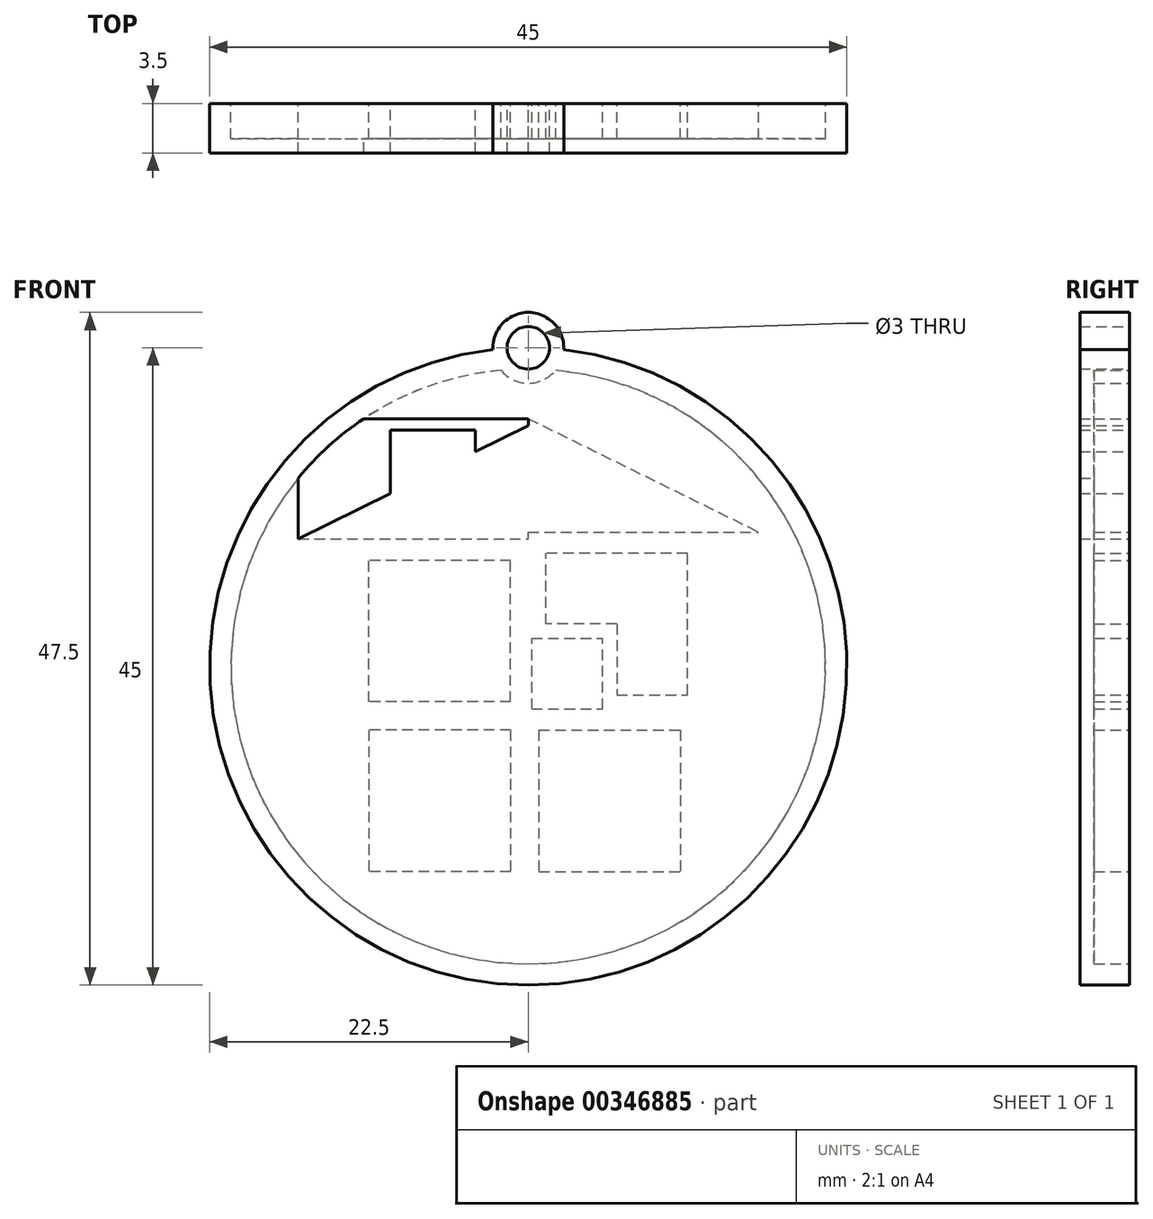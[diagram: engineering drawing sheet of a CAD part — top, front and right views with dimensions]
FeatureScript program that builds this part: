
annotation { "Feature Type Name" : "Feature", "Feature Type Description" : "" }
export const myFeature = defineFeature(function(context is Context, id is Id, definition is map)
    precondition{}
    {
        {
            var Q0;
            Q0=qCreatedBy(makeId("Front.planeOp"),FACE);
            var sketch = newSketch(context, id + "F0", { "sketchPlane" : qUnion([Q0])});
            skLineSegment(sketch, "E0.bottom", {"start": v(0, 0) * mm, "end": v(-10, 0) * mm});
            skLineSegment(sketch, "E0.top", {"start": v(0, 10) * mm, "end": v(-10, 10) * mm});
            skLineSegment(sketch, "E0.left", {"start": v(0, 0) * mm, "end": v(0, 10) * mm});
            skLineSegment(sketch, "E0.right", {"start": v(-10, 0) * mm, "end": v(-10, 10) * mm});
            skLineSegment(sketch, "E1", {"start": v(0, 0) * mm, "end": v(0, -2) * mm});
            skLineSegment(sketch, "E2.bottom", {"start": v(0, -2) * mm, "end": v(-10, -2) * mm});
            skLineSegment(sketch, "E2.top", {"start": v(0, -12) * mm, "end": v(-10, -12) * mm});
            skLineSegment(sketch, "E2.left", {"start": v(0, -2) * mm, "end": v(0, -12) * mm});
            skLineSegment(sketch, "E2.right", {"start": v(-10, -2) * mm, "end": v(-10, -12) * mm});
            skLineSegment(sketch, "E3", {"start": v(0, -2) * mm, "end": v(2, -2) * mm});
            skLineSegment(sketch, "E4.bottom", {"start": v(2, -2) * mm, "end": v(12, -2) * mm});
            skLineSegment(sketch, "E4.top", {"start": v(2, -12) * mm, "end": v(12, -12) * mm});
            skLineSegment(sketch, "E4.left", {"start": v(2, -2) * mm, "end": v(2, -12) * mm});
            skLineSegment(sketch, "E4.right", {"start": v(12, -2) * mm, "end": v(12, -12) * mm});
            skLineSegment(sketch, "E5", {"start": v(2, -2) * mm, "end": v(2, -0.5) * mm});
            skLineSegment(sketch, "E6", {"start": v(0, 0) * mm, "end": v(1.5, 0) * mm});
            skLineSegment(sketch, "E7", {"start": v(1.5, 0) * mm, "end": v(1.5, -0.5) * mm});
            skLineSegment(sketch, "E8", {"start": v(1.5, -0.5) * mm, "end": v(2, -0.5) * mm});
            skLineSegment(sketch, "E9.bottom", {"start": v(1.5, -0.5) * mm, "end": v(6.5, -0.5) * mm});
            skLineSegment(sketch, "E9.top", {"start": v(1.5, 4.5) * mm, "end": v(6.5, 4.5) * mm});
            skLineSegment(sketch, "E9.left", {"start": v(1.5, -0.5) * mm, "end": v(1.5, 4.5) * mm});
            skLineSegment(sketch, "E9.right", {"start": v(6.5, -0.5) * mm, "end": v(6.5, 4.5) * mm});
            skLineSegment(sketch, "E10", {"start": v(6.5, 4.5) * mm, "end": v(7.5, 4.5) * mm});
            skLineSegment(sketch, "E11", {"start": v(7.5, 4.5) * mm, "end": v(7.5, 5.5) * mm});
            skLineSegment(sketch, "E12.bottom", {"start": v(7.5, 5.5) * mm, "end": v(12.5, 5.5) * mm});
            skLineSegment(sketch, "E12.top", {"start": v(7.5, 10.5) * mm, "end": v(12.5, 10.5) * mm});
            skLineSegment(sketch, "E12.left", {"start": v(7.5, 5.5) * mm, "end": v(7.5, 10.5) * mm});
            skLineSegment(sketch, "E12.right", {"start": v(12.5, 5.5) * mm, "end": v(12.5, 10.5) * mm});
            skLineSegment(sketch, "E13.top", {"start": v(7.5, 0.5) * mm, "end": v(12.5, 0.5) * mm});
            skLineSegment(sketch, "E13.left", {"start": v(7.5, 5.5) * mm, "end": v(7.5, 0.5) * mm});
            skLineSegment(sketch, "E13.right", {"start": v(12.5, 5.5) * mm, "end": v(12.5, 0.5) * mm});
            skLineSegment(sketch, "E14.bottom", {"start": v(7.5, 5.5) * mm, "end": v(2.5, 5.5) * mm});
            skLineSegment(sketch, "E14.top", {"start": v(7.5, 10.5) * mm, "end": v(2.5, 10.5) * mm});
            skLineSegment(sketch, "E14.right", {"start": v(2.5, 5.5) * mm, "end": v(2.5, 10.5) * mm});
            skLineSegment(sketch, "E15", {"start": v(0, 10) * mm, "end": v(0, 11.5) * mm});
            skLineSegment(sketch, "E16", {"start": v(2.5, 10.5) * mm, "end": v(2.5, 12) * mm});
            skLineSegment(sketch, "E17", {"start": v(2.5, 12) * mm, "end": v(1.25, 12) * mm});
            skLineSegment(sketch, "E18", {"start": v(0, 11.5) * mm, "end": v(1.25, 11.5) * mm});
            skLineSegment(sketch, "E19", {"start": v(1.25, 11.5) * mm, "end": v(1.25, 12) * mm});
            skLineSegment(sketch, "E20", {"start": v(2.5, 12) * mm, "end": v(17.5, 12) * mm});
            skLineSegment(sketch, "E21", {"start": v(0, 11.5) * mm, "end": v(-15, 11.5) * mm});
            skLineSegment(sketch, "E22", {"start": v(1.25, 12) * mm, "end": v(1.25, 20) * mm});
            skLineSegment(sketch, "E23", {"start": v(1.25, 20) * mm, "end": v(17.5, 12) * mm});
            skLineSegment(sketch, "E24", {"start": v(1.25, 20) * mm, "end": v(1.25, 19.5) * mm});
            skLineSegment(sketch, "E25", {"start": v(-15, 11.5) * mm, "end": v(1.25, 19.5) * mm});
            skLineSegment(sketch, "E26", {"start": v(-10, 10) * mm, "end": v(-7.5, 10) * mm});
            skLineSegment(sketch, "E27", {"start": v(-8.5, 19.2) * mm, "end": v(-2.5, 19.2) * mm});
            skLineSegment(sketch, "E28", {"start": v(-2.5, 19.2) * mm, "end": v(-2.5, 17.65) * mm});
            skLineSegment(sketch, "E29", {"start": v(-8.5, 19.2) * mm, "end": v(-8.5, 14.7) * mm});
            skLineSegment(sketch, "E30", {"start": v(0, 0) * mm, "end": v(0, -1) * mm});
            skLineSegment(sketch, "E31", {"start": v(0, -1) * mm, "end": v(1, -1) * mm});
            skLineSegment(sketch, "E32", {"start": v(1.25, 20) * mm, "end": v(-15, 20) * mm});
            skLineSegment(sketch, "E33", {"start": v(-10, -12) * mm, "end": v(-21.8, -12) * mm});
            skLineSegment(sketch, "E34", {"start": v(-15, 20) * mm, "end": v(-15, -12) * mm});
            skLineSegment(sketch, "E35", {"start": v(-15, -12) * mm, "end": v(-15, 4) * mm});
            skCircle(sketch, "E36", {"center": v(1.25, 2.5) * mm, "radius": 21 * mm});
            skCircle(sketch, "E37", {"center": v(1.25, 2.5) * mm, "radius": 22.5 * mm});
            skLineSegment(sketch, "E38", {"start": v(1.25, 20) * mm, "end": v(1.25, 25) * mm});
            skCircle(sketch, "E39", {"center": v(1.25, 25) * mm, "radius": 1.5 * mm});
            skCircle(sketch, "E40", {"center": v(1.25, 25) * mm, "radius": 2.5 * mm});
            skLineSegment(sketch, "E41", {"start": v(1.25, 2.5) * mm, "end": v(1.25, 11.5) * mm});
            skSolve(sketch);
        }
        {
            var Q0;
            {var subQ0=sQuery(id+"F0.wireOp",EDGE,"E37");var subQ1=sQuery(id+"F0.wireOp",EDGE,"E32");var subQ2=makeQuery(id+"F0.imprint","INTERSECT",VERTEX,{"derivedFrom":[subQ1,subQ0]});Q0=makeQuery(id+"F0.imprint","IMPRINT",FACE,{"disambiguationData":[TD([[makeQuery(id+"F0.imprint","IMPRINT",EDGE,{"disambiguationData":[TD([[subQ2,1.0]])],"derivedFrom":subQ1}),-1.0]])]});}
            var Q1;
            {var subQ0=sQuery(id+"F0.wireOp",EDGE,"E40");var subQ1=sQuery(id+"F0.wireOp",EDGE,"E37");var subQ2=makeQuery(id+"F0.imprint","INTERSECT",VERTEX,{"disambiguationData":[OD(0.0)],"derivedFrom":[subQ1,subQ0]});Q1=makeQuery(id+"F0.imprint","IMPRINT",FACE,{"disambiguationData":[TD([[makeQuery(id+"F0.imprint","IMPRINT",EDGE,{"disambiguationData":[TD([[subQ2,-1.0]])],"derivedFrom":subQ1}),-1.0]])]});}
            var Q2;
            {var subQ0=sQuery(id+"F0.wireOp",EDGE,"E40");var subQ5=sQuery(id+"F0.wireOp",EDGE,"E37");var subQ7=makeQuery(id+"F0.imprint","INTERSECT",VERTEX,{"disambiguationData":[OD(0.0)],"derivedFrom":[subQ5,subQ0]});Q2=makeQuery(id+"F0.imprint","IMPRINT",FACE,{"disambiguationData":[TD([[makeQuery(id+"F0.imprint","IMPRINT",EDGE,{"disambiguationData":[TD([[subQ7,-1.0]])],"derivedFrom":subQ5}),1.0]])]});}
            var Q3;
            {var subQ0=sQuery(id+"F0.wireOp",EDGE,"E40");var subQ5=sQuery(id+"F0.wireOp",EDGE,"E37");var subQ6=makeQuery(id+"F0.imprint","INTERSECT",VERTEX,{"disambiguationData":[OD(1.0)],"derivedFrom":[subQ5,subQ0]});Q3=makeQuery(id+"F0.imprint","IMPRINT",FACE,{"disambiguationData":[TD([[makeQuery(id+"F0.imprint","IMPRINT",EDGE,{"disambiguationData":[TD([[subQ6,1.0]])],"derivedFrom":subQ5}),1.0]])]});}
            var Q4;
            {var subQ0=sQuery(id+"F0.wireOp",EDGE,"E40");var subQ1=sQuery(id+"F0.wireOp",EDGE,"E36");var subQ2=makeQuery(id+"F0.imprint","INTERSECT",VERTEX,{"disambiguationData":[OD(1.0)],"derivedFrom":[subQ1,subQ0]});Q4=makeQuery(id+"F0.imprint","IMPRINT",FACE,{"disambiguationData":[TD([[makeQuery(id+"F0.imprint","IMPRINT",EDGE,{"disambiguationData":[TD([[subQ2,-1.0]])],"derivedFrom":subQ0}),1.0]])]});}
            var Q5;
            {var subQ0=sQuery(id+"F0.wireOp",EDGE,"E40");var subQ1=sQuery(id+"F0.wireOp",EDGE,"E36");var subQ2=makeQuery(id+"F0.imprint","INTERSECT",VERTEX,{"disambiguationData":[OD(0.0)],"derivedFrom":[subQ1,subQ0]});Q5=makeQuery(id+"F0.imprint","IMPRINT",FACE,{"disambiguationData":[TD([[makeQuery(id+"F0.imprint","IMPRINT",EDGE,{"disambiguationData":[TD([[subQ2,1.0]])],"derivedFrom":subQ0}),1.0]])]});}
            var Q6;
            {var subQ1=sQuery(id+"F0.wireOp",EDGE,"E32");var subQ3=sQuery(id+"F0.wireOp",EDGE,"E36");var subQ4=makeQuery(id+"F0.imprint","INTERSECT",VERTEX,{"derivedFrom":[subQ1,subQ3]});Q6=makeQuery(id+"F0.imprint","IMPRINT",FACE,{"disambiguationData":[TD([[makeQuery(id+"F0.imprint","IMPRINT",EDGE,{"disambiguationData":[TD([[subQ4,1.0]])],"derivedFrom":subQ3}),1.0]])]});}
            var Q7;
            {var subQ10=sQuery(id+"F0.wireOp",EDGE,"E2.top");Q7=makeQuery(id+"F0.imprint","IMPRINT",FACE,{"disambiguationData":[TD([[makeQuery(id+"F0.imprint","IMPRINT",EDGE,{"derivedFrom":subQ10}),1.0]])]});}
            var Q8;
            {var subQ0=sQuery(id+"F0.wireOp",EDGE,"E37");var subQ1=sQuery(id+"F0.wireOp",EDGE,"E33");var subQ2=makeQuery(id+"F0.imprint","INTERSECT",VERTEX,{"derivedFrom":[subQ1,subQ0]});Q8=makeQuery(id+"F0.imprint","IMPRINT",FACE,{"disambiguationData":[TD([[makeQuery(id+"F0.imprint","IMPRINT",EDGE,{"disambiguationData":[TD([[subQ2,1.0]])],"derivedFrom":subQ1}),1.0]])]});}
            var Q9;
            Q9=makeQuery(id+"F0.imprint","IMPRINT",FACE,{"disambiguationData":[TD([[makeQuery(id+"F0.imprint","IMPRINT",EDGE,{"derivedFrom":sQuery(id+"F0.wireOp",EDGE,"E18")}),1.0]])]});
            var Q10;
            Q10=makeQuery(id+"F0.imprint","IMPRINT",FACE,{"disambiguationData":[TD([[makeQuery(id+"F0.imprint","IMPRINT",EDGE,{"derivedFrom":sQuery(id+"F0.wireOp",EDGE,"E17")}),-1.0]])]});
            var Q11;
            Q11=makeQuery(id+"F0.imprint","IMPRINT",FACE,{"disambiguationData":[TD([[makeQuery(id+"F0.imprint","IMPRINT",EDGE,{"derivedFrom":sQuery(id+"F0.wireOp",EDGE,"E14.bottom")}),-1.0]])]});
            var Q12;
            Q12=makeQuery(id+"F0.imprint","IMPRINT",FACE,{"disambiguationData":[TD([[makeQuery(id+"F0.imprint","IMPRINT",EDGE,{"derivedFrom":sQuery(id+"F0.wireOp",EDGE,"E12.top")}),-1.0]])]});
            var Q13;
            {var subQ3=sQuery(id+"F0.wireOp",EDGE,"E12.bottom");Q13=makeQuery(id+"F0.imprint","IMPRINT",FACE,{"disambiguationData":[TD([[makeQuery(id+"F0.imprint","IMPRINT",EDGE,{"derivedFrom":subQ3}),-1.0]])]});}
            var Q14;
            {var subQ4=sQuery(id+"F0.wireOp",EDGE,"E9.top");Q14=makeQuery(id+"F0.imprint","IMPRINT",FACE,{"disambiguationData":[TD([[makeQuery(id+"F0.imprint","IMPRINT",EDGE,{"derivedFrom":subQ4}),-1.0]])]});}
            var Q15;
            {var subQ4=sQuery(id+"F0.wireOp",EDGE,"E6");Q15=makeQuery(id+"F0.imprint","IMPRINT",FACE,{"disambiguationData":[TD([[makeQuery(id+"F0.imprint","IMPRINT",EDGE,{"derivedFrom":subQ4}),1.0]])]});}
            var Q16;
            Q16=makeQuery(id+"F0.imprint","IMPRINT",FACE,{"disambiguationData":[TD([[makeQuery(id+"F0.imprint","IMPRINT",EDGE,{"derivedFrom":sQuery(id+"F0.wireOp",EDGE,"E1")}),1.0]])]});
            var Q17;
            Q17=makeQuery(id+"F0.imprint","IMPRINT",FACE,{"disambiguationData":[TD([[makeQuery(id+"F0.imprint","IMPRINT",EDGE,{"derivedFrom":sQuery(id+"F0.wireOp",EDGE,"E4.bottom")}),-1.0]])]});
            var Q18;
            Q18=makeQuery(id+"F0.imprint","IMPRINT",FACE,{"disambiguationData":[TD([[makeQuery(id+"F0.imprint","IMPRINT",EDGE,{"derivedFrom":sQuery(id+"F0.wireOp",EDGE,"E2.bottom")}),1.0]])]});
            var Q19;
            {var subQ1=sQuery(id+"F0.wireOp",EDGE,"E0.bottom");Q19=makeQuery(id+"F0.imprint","IMPRINT",FACE,{"disambiguationData":[TD([[makeQuery(id+"F0.imprint","IMPRINT",EDGE,{"derivedFrom":subQ1}),1.0]])]});}
            var Q20;
            {var subQ0=sQuery(id+"F0.wireOp",EDGE,"E0.bottom");Q20=makeQuery(id+"F0.imprint","IMPRINT",FACE,{"disambiguationData":[TD([[makeQuery(id+"F0.imprint","IMPRINT",EDGE,{"derivedFrom":subQ0}),-1.0]])]});}
            var Q21;
            {var subQ5=sQuery(id+"F0.wireOp",EDGE,"E0.top");Q21=makeQuery(id+"F0.imprint","IMPRINT",FACE,{"disambiguationData":[TD([[makeQuery(id+"F0.imprint","IMPRINT",EDGE,{"derivedFrom":subQ5}),1.0]])]});}
            var Q22;
            Q22=makeQuery(id+"F0.imprint","IMPRINT",FACE,{"disambiguationData":[TD([[makeQuery(id+"F0.imprint","IMPRINT",EDGE,{"derivedFrom":sQuery(id+"F0.wireOp",EDGE,"E0.top")}),-1.0]])]});
            var Q23;
            {var subQ1=sQuery(id+"F0.wireOp",EDGE,"E24");Q23=makeQuery(id+"F0.imprint","IMPRINT",FACE,{"disambiguationData":[TD([[makeQuery(id+"F0.imprint","IMPRINT",EDGE,{"derivedFrom":subQ1}),-1.0]])]});}
            var Q24;
            Q24=makeQuery(id+"F0.imprint","IMPRINT",FACE,{"disambiguationData":[TD([[makeQuery(id+"F0.imprint","IMPRINT",EDGE,{"derivedFrom":sQuery(id+"F0.wireOp",EDGE,"E27")}),-1.0]])]});
            var Q25;
            {var subQ0=sQuery(id+"F0.wireOp",EDGE,"E37");var subQ1=sQuery(id+"F0.wireOp",EDGE,"E32");var subQ2=makeQuery(id+"F0.imprint","INTERSECT",VERTEX,{"derivedFrom":[subQ1,subQ0]});Q25=makeQuery(id+"F0.imprint","IMPRINT",FACE,{"disambiguationData":[TD([[makeQuery(id+"F0.imprint","IMPRINT",EDGE,{"disambiguationData":[TD([[subQ2,1.0]])],"derivedFrom":subQ1}),1.0]])]});}
            var Q26;
            {var subQ0=sQuery(id+"F0.wireOp",EDGE,"E37");var subQ1=sQuery(id+"F0.wireOp",EDGE,"E34");var subQ2=makeQuery(id+"F0.imprint","INTERSECT",VERTEX,{"derivedFrom":[subQ1,subQ0]});Q26=makeQuery(id+"F0.imprint","IMPRINT",FACE,{"disambiguationData":[TD([[makeQuery(id+"F0.imprint","IMPRINT",EDGE,{"disambiguationData":[TD([[subQ2,-1.0]])],"derivedFrom":subQ1}),-1.0]])]});}
            var Q27;
            {var subQ0=sQuery(id+"F0.wireOp",EDGE,"E34");var subQ2=sQuery(id+"F0.wireOp",EDGE,"E36");var subQ3=makeQuery(id+"F0.imprint","INTERSECT",VERTEX,{"derivedFrom":[subQ0,subQ2]});Q27=makeQuery(id+"F0.imprint","IMPRINT",FACE,{"disambiguationData":[TD([[makeQuery(id+"F0.imprint","IMPRINT",EDGE,{"disambiguationData":[TD([[subQ3,-1.0]])],"derivedFrom":subQ2}),1.0]])]});}
            var Q28;
            {var subQ0=sQuery(id+"F0.wireOp",EDGE,"E37");var subQ1=sQuery(id+"F0.wireOp",EDGE,"E33");var subQ2=makeQuery(id+"F0.imprint","INTERSECT",VERTEX,{"derivedFrom":[subQ1,subQ0]});Q28=makeQuery(id+"F0.imprint","IMPRINT",FACE,{"disambiguationData":[TD([[makeQuery(id+"F0.imprint","IMPRINT",EDGE,{"disambiguationData":[TD([[subQ2,1.0]])],"derivedFrom":subQ1}),-1.0]])]});}
            var Q29;
            {var subQ0=sQuery(id+"F0.wireOp",EDGE,"E35");var subQ1=sQuery(id+"F0.wireOp",EDGE,"E33");var subQ2=makeQuery(id+"F0.imprint","INTERSECT",VERTEX,{"derivedFrom":[subQ1,subQ0]});Q29=makeQuery(id+"F0.imprint","IMPRINT",FACE,{"disambiguationData":[TD([[makeQuery(id+"F0.imprint","IMPRINT",EDGE,{"disambiguationData":[TD([[subQ2,1.0]])],"derivedFrom":subQ1}),-1.0]])]});}
            extrude(context, id + "F1", {"entities" : qUnion([Q0, Q1, Q2, Q3, Q4, Q5, Q6, Q7, Q8, Q9, Q10, Q11, Q12, Q13, Q14, Q15, Q16, Q17, Q18, Q19, Q20, Q21, Q22, Q23, Q24, Q25, Q26, Q27, Q28, Q29]), "depth" : 3.5 * mm});
        }
        {
            var Q0;
            {var subQ10=sQuery(id+"F0.wireOp",EDGE,"E2.top");Q0=makeQuery(id+"F0.imprint","IMPRINT",FACE,{"disambiguationData":[TD([[makeQuery(id+"F0.imprint","IMPRINT",EDGE,{"derivedFrom":subQ10}),1.0]])]});}
            var Q1;
            {var subQ4=sQuery(id+"F0.wireOp",EDGE,"E6");Q1=makeQuery(id+"F0.imprint","IMPRINT",FACE,{"disambiguationData":[TD([[makeQuery(id+"F0.imprint","IMPRINT",EDGE,{"derivedFrom":subQ4}),1.0]])]});}
            var Q2;
            Q2=makeQuery(id+"F0.imprint","IMPRINT",FACE,{"disambiguationData":[TD([[makeQuery(id+"F0.imprint","IMPRINT",EDGE,{"derivedFrom":sQuery(id+"F0.wireOp",EDGE,"E1")}),1.0]])]});
            var Q3;
            {var subQ1=sQuery(id+"F0.wireOp",EDGE,"E0.bottom");Q3=makeQuery(id+"F0.imprint","IMPRINT",FACE,{"disambiguationData":[TD([[makeQuery(id+"F0.imprint","IMPRINT",EDGE,{"derivedFrom":subQ1}),1.0]])]});}
            var Q4;
            Q4=makeQuery(id+"F0.imprint","IMPRINT",FACE,{"disambiguationData":[TD([[makeQuery(id+"F0.imprint","IMPRINT",EDGE,{"derivedFrom":sQuery(id+"F0.wireOp",EDGE,"E0.top")}),-1.0]])]});
            var Q5;
            {var subQ0=sQuery(id+"F0.wireOp",EDGE,"E34");var subQ2=sQuery(id+"F0.wireOp",EDGE,"E36");var subQ3=makeQuery(id+"F0.imprint","INTERSECT",VERTEX,{"derivedFrom":[subQ0,subQ2]});Q5=makeQuery(id+"F0.imprint","IMPRINT",FACE,{"disambiguationData":[TD([[makeQuery(id+"F0.imprint","IMPRINT",EDGE,{"disambiguationData":[TD([[subQ3,-1.0]])],"derivedFrom":subQ2}),1.0]])]});}
            var Q6;
            {var subQ1=sQuery(id+"F0.wireOp",EDGE,"E24");Q6=makeQuery(id+"F0.imprint","IMPRINT",FACE,{"disambiguationData":[TD([[makeQuery(id+"F0.imprint","IMPRINT",EDGE,{"derivedFrom":subQ1}),-1.0]])]});}
            var Q7;
            {var subQ1=sQuery(id+"F0.wireOp",EDGE,"E32");var subQ3=sQuery(id+"F0.wireOp",EDGE,"E36");var subQ4=makeQuery(id+"F0.imprint","INTERSECT",VERTEX,{"derivedFrom":[subQ1,subQ3]});Q7=makeQuery(id+"F0.imprint","IMPRINT",FACE,{"disambiguationData":[TD([[makeQuery(id+"F0.imprint","IMPRINT",EDGE,{"disambiguationData":[TD([[subQ4,1.0]])],"derivedFrom":subQ3}),1.0]])]});}
            extrude(context, id + "F2", {"entities" : qUnion([Q0, Q1, Q2, Q3, Q4, Q5, Q6, Q7]), "operationType" : NewBodyOperationType.REMOVE, "depth" : 2.5 * mm});
        }
    });
